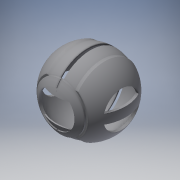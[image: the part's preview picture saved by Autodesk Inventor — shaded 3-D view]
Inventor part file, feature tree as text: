
AUTODESK INVENTOR PART (.ipt)
format: ipt  version: 2019 (Build 230136000, 136)  size: 381,440 bytes
history: native  units: in
note: dims shown in document units (in); Inventor stores cm internally (conversion verified against a paired STEP export)
features: sketch x16, plane x7, extrude x7, revolve x5, mirror x3, projected_geometry x2, shell x1, chamfer x1
ambient origin geometry x8: Origin, YZ Plane, XZ Plane, XY Plane, X Axis, Y Axis, Z Axis, Center Point
bodies: Solid1 (feature_tree)
feature tree (42):
  revolve  "Revolution1"  Angle=90.0deg
  plane  "Work Plane1"
  extrude  "Extrusion1"  Depth=3.0in
  shell  "Shell2"  Thickness=3.0in
  plane  "Work Plane2"
  extrude  "Extrusion2"  Depth=0.2in
  chamfer  "Chamfer1"  Distance=1.125in
  plane  "Work Plane3"
  extrude  "Extrusion3"  Depth=3.15in
  extrude  "Extrusion4"  Depth=1.5in TaperAngle=0.0deg
  extrude  "Extrusion5"  Depth=3.1in
  revolve  "Revolution2"  [1 undecoded]
  mirror  "Mirror1"
  mirror  "Mirror2"
  extrude  "Extrusion6"  Depth=3.0in
  plane  "Work Plane4"
  plane  "Work Plane5"
  extrude  "Extrusion7"  Depth=0.8in
  mirror  "Mirror3"
  revolve  "Revolution3"  [1 undecoded]
  sketch  "Sketch13"  dims[d31=3.0in d32=-3.125in d33=3.0in]
  sketch  "Sketch14"  dims[d34=0.4in d35=0.8in]
  sketch  "Sketch18"  dims[d36=1.8125in d37=0.0in d39=5.8in]
  plane  "Work Plane7"
  revolve  "Revolution5"  [1 undecoded]
  sketch  "Sketch20"  dims[d50=0.025in d51=2.0958in]
  plane  "Work Plane8"
  revolve  "Revolution6"  [1 undecoded]
  sketch  "Sketch1"  dims[d0=6.0in d1=90.0deg]
  sketch  "Sketch2"  dims[d2=3.0in d5=1.0in d7=3.0in]
  sketch  "Sketch3"  dims[d8=1.625in d9=0.0in d11=0.2in]
  sketch  "Sketch4"  dims[d12=-0.25in]
  sketch  "Sketch5"  dims[d13=3.0in]
  sketch  "Sketch6"  dims[d14=4.0in d15=1.125in d16=0.0in]
  projected_geometry  "Projected Loop1"
  sketch  "Sketch7"  dims[d17=0.5in d18=0.125in d19=0.2542in d20=3.15in]
  sketch  "Sketch8"  dims[d21=2.4375in d22=0.0in d23=1.5in d24=0.0in]
  sketch  "Sketch11"  dims[d25=3.9375in d26=0.0in d27=3.1in]
  sketch  "Sketch12"  dims[d28=90.0deg d29=5.0625in d30=0.0in]
  sketch  "Sketch19"  dims[d40=285.0deg d49=0.05in]
  sketch  "Sketch21"  dims[d52=0.2873in d53=6.0in d54=0.1in d55=0.125in d56=0.11in d57=1.8991in d58=0.25in]
  projected_geometry  "Projected Loop2"
note: 4 required parameter values undecoded (feature->parameter linkage not recoverable at this tier; creation-order binding heuristic only, values carry confidence <= 0.55)
